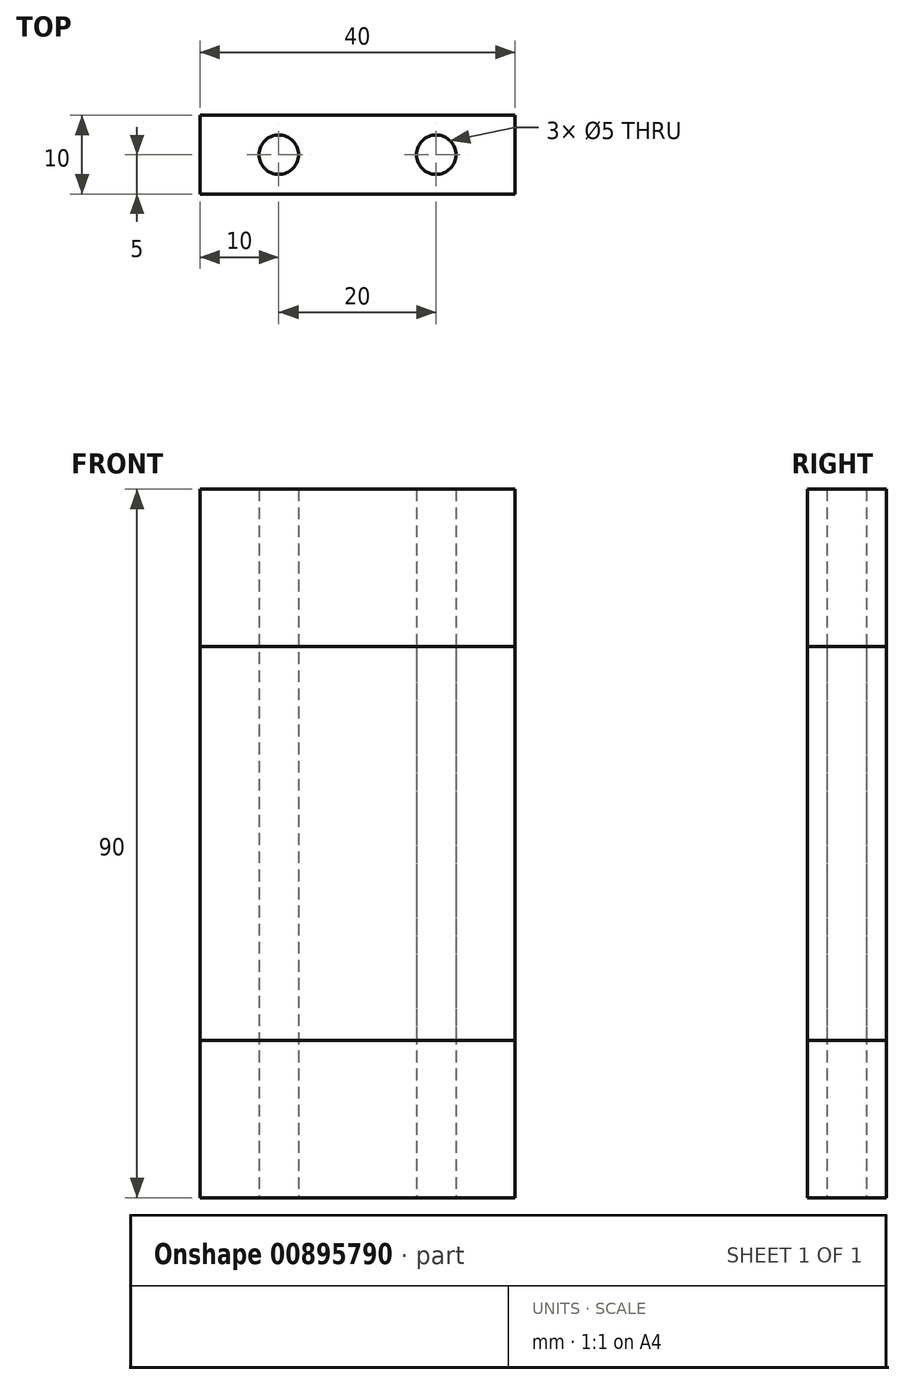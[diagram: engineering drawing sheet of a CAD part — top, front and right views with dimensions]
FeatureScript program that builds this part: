
annotation { "Feature Type Name" : "Feature", "Feature Type Description" : "" }
export const myFeature = defineFeature(function(context is Context, id is Id, definition is map)
    precondition{}
    {
        {
            var Q0;
            Q0=qCreatedBy(makeId("Top.planeOp"),FACE);
            var sketch = newSketch(context, id + "F0", { "sketchPlane" : qUnion([Q0])});
            skLineSegment(sketch, "E0.bottom", {"start": v(-20, 5) * mm, "end": v(20, 5) * mm});
            skLineSegment(sketch, "E0.top", {"start": v(-20, -5) * mm, "end": v(20, -5) * mm});
            skLineSegment(sketch, "E0.left", {"start": v(-20, 5) * mm, "end": v(-20, -5) * mm});
            skLineSegment(sketch, "E0.right", {"start": v(20, 5) * mm, "end": v(20, -5) * mm});
            skPoint(sketch, "E0.middle", {"position": v(0, 0) * mm});
            skCircle(sketch, "E1", {"center": v(-10, 0) * mm, "radius": 2.5 * mm});
            skCircle(sketch, "E2.MirrorC", {"center": v(10, 0) * mm, "radius": 2.5 * mm});
            skSolve(sketch);
        }
        {
            var Q0;
            Q0=makeQuery(id+"F0.imprint","IMPRINT",FACE,{"disambiguationData":[TD([[makeQuery(id+"F0.imprint","IMPRINT",EDGE,{"derivedFrom":sQuery(id+"F0.wireOp",EDGE,"E0.bottom")}),-1.0]])]});
            extrude(context, id + "F1", {"entities" : qUnion([Q0]), "depth" : 45 * mm, "offsetDistance" : 25 * mm, "hasSecondDirection" : true, "secondDirectionOppositeDirection" : true, "secondDirectionDepth" : 45 * mm});
        }
        {
            var Q0;
            Q0=makeQuery(id+"F0.imprint","IMPRINT",FACE,{"disambiguationData":[TD([[makeQuery(id+"F0.imprint","IMPRINT",EDGE,{"derivedFrom":sQuery(id+"F0.wireOp",EDGE,"E1")}),1.0]])]});
            var Q1;
            Q1=makeQuery(id+"F0.imprint","IMPRINT",FACE,{"disambiguationData":[TD([[makeQuery(id+"F0.imprint","IMPRINT",EDGE,{"derivedFrom":sQuery(id+"F0.wireOp",EDGE,"E2.MirrorC")}),-1.0]])]});
            extrude(context, id + "F2", {"entities" : qUnion([Q0, Q1]), "depth" : 25 * mm, "offsetDistance" : 25 * mm, "hasSecondDirection" : true, "secondDirectionOppositeDirection" : true, "secondDirectionDepth" : 25 * mm});
        }
    });
